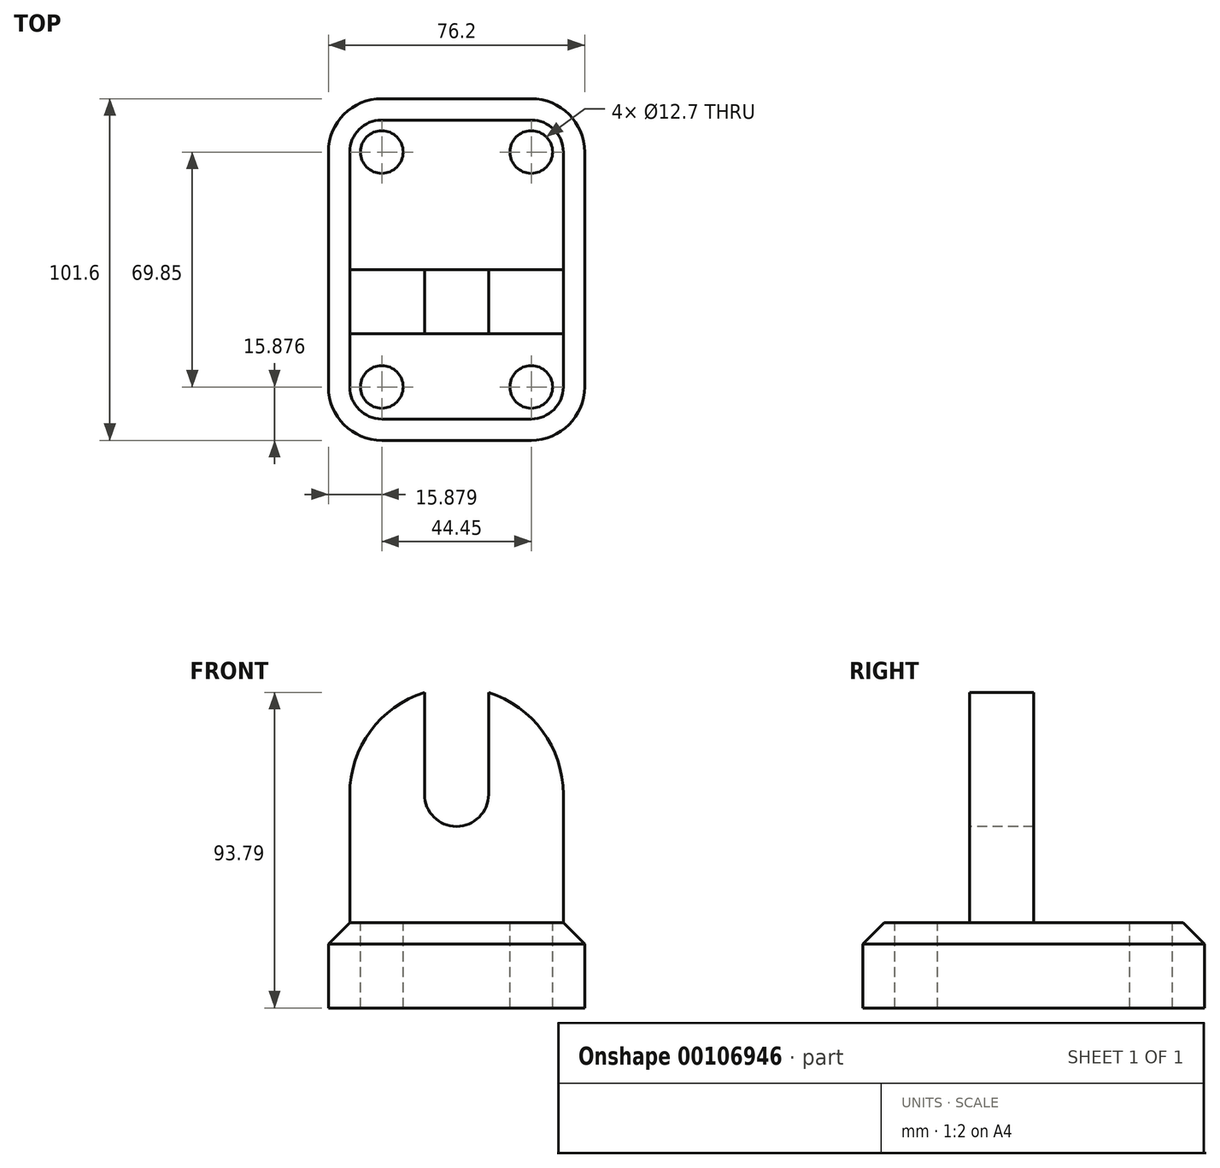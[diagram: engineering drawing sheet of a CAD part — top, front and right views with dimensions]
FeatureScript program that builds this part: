
annotation { "Feature Type Name" : "Feature", "Feature Type Description" : "" }
export const myFeature = defineFeature(function(context is Context, id is Id, definition is map)
    precondition{}
    {
        {
            var Q0;
            Q0=qCreatedBy(makeId("Top.planeOp"),FACE);
            var sketch = newSketch(context, id + "F0", { "sketchPlane" : qUnion([Q0])});
            skLineSegment(sketch, "E0.bottom", {"start": v(-44.67, 51.36) * mm, "end": v(31.53, 51.36) * mm});
            skLineSegment(sketch, "E0.top", {"start": v(-44.67, -50.24) * mm, "end": v(31.53, -50.24) * mm});
            skLineSegment(sketch, "E0.left", {"start": v(-44.67, 51.36) * mm, "end": v(-44.67, -50.24) * mm});
            skLineSegment(sketch, "E0.right", {"start": v(31.53, 51.36) * mm, "end": v(31.53, -50.24) * mm});
            skSolve(sketch);
        }
        {
            var Q0;
            Q0 = qSketchRegion(id + "F0", true);
            extrude(context, id + "F1", {"entities" : qUnion([Q0]), "depth" : 25.4 * mm});
        }
        {
            var Q0;
            Q0=makeQuery(id+"F1.opExtrude","CAP_FACE",FACE,{"disambiguationData":[OSD([sQuery(id+"F0.wireOp",EDGE,"E0.bottom"),sQuery(id+"F0.wireOp",EDGE,"E0.top"),sQuery(id+"F0.wireOp",EDGE,"E0.left"),sQuery(id+"F0.wireOp",EDGE,"E0.right")])],"isStart":false});
            var sketch = newSketch(context, id + "F2", { "sketchPlane" : qUnion([Q0])});
            skLineSegment(sketch, "E1", {"start": v(31.53, 51.36) * mm, "end": v(31.53, 0.56) * mm});
            skLineSegment(sketch, "E2", {"start": v(25.18, 0.56) * mm, "end": v(25.18, -18.49) * mm});
            skLineSegment(sketch, "E3", {"start": v(25.18, 0.56) * mm, "end": v(-38.32, 0.56) * mm});
            skLineSegment(sketch, "E4", {"start": v(-38.32, 0.56) * mm, "end": v(-38.32, -18.49) * mm});
            skLineSegment(sketch, "E5", {"start": v(-38.32, -18.49) * mm, "end": v(25.18, -18.49) * mm});
            skSolve(sketch);
        }
        {
            var Q0;
            Q0 = qSketchRegion(id + "F2", true);
            extrude(context, id + "F3", {"entities" : qUnion([Q0]), "operationType" : NewBodyOperationType.ADD, "depth" : 76.2 * mm});
        }
        {
            var Q0;
            Q0=makeQuery(id+"F3.opExtrude","SWEPT_FACE",FACE,{"disambiguationData":[OSD([sQuery(id+"F2.wireOp",EDGE,"E5")])]});
            var sketch = newSketch(context, id + "F4", { "sketchPlane" : qUnion([Q0])});
            skLineSegment(sketch, "E6", {"start": v(25.18, 25.4) * mm, "end": v(-6.57, 25.4) * mm});
            skLineSegment(sketch, "E7", {"start": v(-6.57, 25.4) * mm, "end": v(-6.57, 63.5) * mm});
            skCircle(sketch, "E8", {"center": v(-6.57, 63.5) * mm, "radius": 9.53 * mm});
            skCircle(sketch, "E9", {"center": v(-6.57, 63.5) * mm, "radius": 31.75 * mm});
            skLineSegment(sketch, "E10", {"start": v(2.96, 63.5) * mm, "end": v(2.96, 101.6) * mm});
            skLineSegment(sketch, "E11", {"start": v(-16.1, 63.5) * mm, "end": v(-16.1, 101.6) * mm});
            skSolve(sketch);
        }
        {
            var Q0;
            {var subQ1=sQuery(id+"F2.wireOp",EDGE,"E5");var subQ6=makeQuery(id+"F3.opExtrude","CAP_EDGE",EDGE,{"disambiguationData":[OSD([subQ1])],"isStart":false});Q0=makeQuery(id+"F4.imprint","IMPRINT",FACE,{"disambiguationData":[TD([[makeQuery(id+"F4.imprint","IMPRINT",EDGE,{"derivedFrom":subQ6}),-1.0]])]});}
            extrude(context, id + "F5", {"entities" : qUnion([Q0]), "operationType" : NewBodyOperationType.REMOVE, "oppositeDirection" : true, "depth" : 54.6 * mm});
        }
        {
            var Q0;
            {var subQ0=sQuery(id+"F4.wireOp",EDGE,"E10");var subQ1=sQuery(id+"F4.wireOp",EDGE,"E8");var subQ2=makeQuery(id+"F4.imprint","INTERSECT",VERTEX,{"derivedFrom":[subQ1,subQ0]});Q0=makeQuery(id+"F4.imprint","IMPRINT",FACE,{"disambiguationData":[TD([[makeQuery(id+"F4.imprint","IMPRINT",EDGE,{"disambiguationData":[TD([[subQ2,-1.0]])],"derivedFrom":subQ1}),-1.0]])]});}
            var Q1;
            {var subQ0=sQuery(id+"F4.wireOp",EDGE,"E8");var subQ1=makeQuery(id+"F4.imprint","INTERSECT",VERTEX,{"derivedFrom":[subQ0,sQuery(id+"F4.wireOp",EDGE,"E10")]});Q1=makeQuery(id+"F4.imprint","IMPRINT",FACE,{"disambiguationData":[TD([[makeQuery(id+"F4.imprint","IMPRINT",EDGE,{"disambiguationData":[TD([[subQ1,-1.0]])],"derivedFrom":subQ0}),1.0]])]});}
            extrude(context, id + "F6", {"entities" : qUnion([Q0, Q1]), "operationType" : NewBodyOperationType.REMOVE, "oppositeDirection" : true, "depth" : 25.4 * mm});
        }
        {
            var Q0;
            Q0=makeQuery(id+"F1.opExtrude","CAP_FACE",FACE,{"disambiguationData":[OSD([sQuery(id+"F0.wireOp",EDGE,"E0.bottom"),sQuery(id+"F0.wireOp",EDGE,"E0.top"),sQuery(id+"F0.wireOp",EDGE,"E0.left"),sQuery(id+"F0.wireOp",EDGE,"E0.right")])],"isStart":false});
            var sketch = newSketch(context, id + "F7", { "sketchPlane" : qUnion([Q0])});
            skPoint(sketch, "E12", {"position": v(15.66, -34.36) * mm});
            skPoint(sketch, "E13", {"position": v(-28.8, -34.36) * mm});
            skCircle(sketch, "E14", {"center": v(15.66, -34.36) * mm, "radius": 6.35 * mm});
            skCircle(sketch, "E15", {"center": v(-28.8, -34.36) * mm, "radius": 6.35 * mm});
            skPoint(sketch, "E16", {"position": v(15.66, 35.49) * mm});
            skPoint(sketch, "E17", {"position": v(-28.8, 35.49) * mm});
            skCircle(sketch, "E18", {"center": v(-28.8, 35.49) * mm, "radius": 6.35 * mm});
            skCircle(sketch, "E19", {"center": v(15.66, 35.49) * mm, "radius": 6.35 * mm});
            skCircle(sketch, "E20", {"center": v(-28.8, 35.49) * mm, "radius": 15.88 * mm});
            skCircle(sketch, "E21", {"center": v(15.66, 35.49) * mm, "radius": 15.88 * mm});
            skCircle(sketch, "E22", {"center": v(15.66, -34.36) * mm, "radius": 15.88 * mm});
            skCircle(sketch, "E23", {"center": v(-28.8, -34.36) * mm, "radius": 15.88 * mm});
            skSolve(sketch);
        }
        {
            var Q0;
            Q0=sQuery(id+"F7.wireOp",VERTEX,"E17");
            var Q1;
            Q1=sQuery(id+"F7.wireOp",VERTEX,"E16");
            var Q2;
            Q2=sQuery(id+"F7.wireOp",VERTEX,"E12");
            var Q3;
            Q3=sQuery(id+"F7.wireOp",VERTEX,"E13");
            var Q4;
            Q4=makeQuery(id+"F1.opExtrude","SWEPT_BODY",BODY,{"disambiguationData":[OSD([sQuery(id+"F0.wireOp",EDGE,"E0.bottom"),sQuery(id+"F0.wireOp",EDGE,"E0.top"),sQuery(id+"F0.wireOp",EDGE,"E0.left"),sQuery(id+"F0.wireOp",EDGE,"E0.right")])]});
            hole(context, id + "F8", {"style" : HoleStyle.SIMPLE, "endStyle" : HoleEndStyle.BLIND, "holeDiameter" : 12.7 * mm, "holeDepth" : 215.9 * mm, "locations" : qUnion([Q0, Q1, Q2, Q3]), "scope" : qUnion([Q4])});
        }
        {
            var Q0;
            {var subQ0=sQuery(id+"F7.wireOp",EDGE,"E20");var subQ1=makeQuery(id+"F1.opExtrude","CAP_EDGE",EDGE,{"disambiguationData":[OSD([sQuery(id+"F0.wireOp",EDGE,"E0.bottom")])],"isStart":false});var subQ2=makeQuery(id+"F7.imprint","INTERSECT",VERTEX,{"derivedFrom":[subQ1,subQ0]});Q0=makeQuery(id+"F7.imprint","IMPRINT",FACE,{"disambiguationData":[TD([[makeQuery(id+"F7.imprint","IMPRINT",EDGE,{"disambiguationData":[TD([[subQ2,-1.0]])],"derivedFrom":subQ0}),-1.0]])]});}
            var Q1;
            {var subQ0=sQuery(id+"F7.wireOp",EDGE,"E21");var subQ1=makeQuery(id+"F1.opExtrude","CAP_EDGE",EDGE,{"disambiguationData":[OSD([sQuery(id+"F0.wireOp",EDGE,"E0.bottom")])],"isStart":false});var subQ2=makeQuery(id+"F7.imprint","INTERSECT",VERTEX,{"derivedFrom":[subQ1,subQ0]});Q1=makeQuery(id+"F7.imprint","IMPRINT",FACE,{"disambiguationData":[TD([[makeQuery(id+"F7.imprint","IMPRINT",EDGE,{"disambiguationData":[TD([[subQ2,1.0]])],"derivedFrom":subQ0}),-1.0]])]});}
            var Q2;
            {var subQ0=sQuery(id+"F7.wireOp",EDGE,"E22");var subQ1=makeQuery(id+"F1.opExtrude","CAP_EDGE",EDGE,{"disambiguationData":[OSD([sQuery(id+"F0.wireOp",EDGE,"E0.right")])],"isStart":false});var subQ2=makeQuery(id+"F7.imprint","INTERSECT",VERTEX,{"derivedFrom":[subQ1,subQ0]});Q2=makeQuery(id+"F7.imprint","IMPRINT",FACE,{"disambiguationData":[TD([[makeQuery(id+"F7.imprint","IMPRINT",EDGE,{"disambiguationData":[TD([[subQ2,1.0]])],"derivedFrom":subQ0}),-1.0]])]});}
            var Q3;
            {var subQ0=sQuery(id+"F7.wireOp",EDGE,"E23");var subQ1=makeQuery(id+"F1.opExtrude","CAP_EDGE",EDGE,{"disambiguationData":[OSD([sQuery(id+"F0.wireOp",EDGE,"E0.left")])],"isStart":false});var subQ2=makeQuery(id+"F7.imprint","INTERSECT",VERTEX,{"derivedFrom":[subQ1,subQ0]});Q3=makeQuery(id+"F7.imprint","IMPRINT",FACE,{"disambiguationData":[TD([[makeQuery(id+"F7.imprint","IMPRINT",EDGE,{"disambiguationData":[TD([[subQ2,-1.0]])],"derivedFrom":subQ0}),-1.0]])]});}
            extrude(context, id + "F9", {"entities" : qUnion([Q0, Q1, Q2, Q3]), "operationType" : NewBodyOperationType.REMOVE, "oppositeDirection" : true, "depth" : 25.4 * mm});
        }
        {
            var Q0;
            Q0=makeQuery(id+"F9.boolean.opBoolean","COPY",EDGE,{"derivedFrom":makeQuery(id+"F9.opExtrude","CAP_EDGE",EDGE,{"disambiguationData":[OSD([sQuery(id+"F7.wireOp",EDGE,"E22")])],"isStart":true})});
            var Q1;
            Q1=makeQuery(id+"F1.opExtrude","CAP_EDGE",EDGE,{"disambiguationData":[OSD([sQuery(id+"F0.wireOp",EDGE,"E0.right")])],"isStart":false});
            var Q2;
            Q2=makeQuery(id+"F9.boolean.opBoolean","COPY",EDGE,{"derivedFrom":makeQuery(id+"F9.opExtrude","CAP_EDGE",EDGE,{"disambiguationData":[OSD([sQuery(id+"F7.wireOp",EDGE,"E21")])],"isStart":true})});
            var Q3;
            Q3=makeQuery(id+"F1.opExtrude","CAP_EDGE",EDGE,{"disambiguationData":[OSD([sQuery(id+"F0.wireOp",EDGE,"E0.bottom")])],"isStart":false});
            var Q4;
            Q4=makeQuery(id+"F9.boolean.opBoolean","COPY",EDGE,{"derivedFrom":makeQuery(id+"F9.opExtrude","CAP_EDGE",EDGE,{"disambiguationData":[OSD([sQuery(id+"F7.wireOp",EDGE,"E20")])],"isStart":true})});
            var Q5;
            Q5=makeQuery(id+"F1.opExtrude","CAP_EDGE",EDGE,{"disambiguationData":[OSD([sQuery(id+"F0.wireOp",EDGE,"E0.left")])],"isStart":false});
            var Q6;
            Q6=makeQuery(id+"F9.boolean.opBoolean","COPY",EDGE,{"derivedFrom":makeQuery(id+"F9.opExtrude","CAP_EDGE",EDGE,{"disambiguationData":[OSD([sQuery(id+"F7.wireOp",EDGE,"E23")])],"isStart":true})});
            var Q7;
            Q7=makeQuery(id+"F1.opExtrude","CAP_EDGE",EDGE,{"disambiguationData":[OSD([sQuery(id+"F0.wireOp",EDGE,"E0.top")])],"isStart":false});
            chamfer(context, id + "F10", {"entities" : qUnion([Q0, Q1, Q2, Q3, Q4, Q5, Q6, Q7]), "width" : 6.35 * mm, "tangentPropagation" : true});
        }
    });
